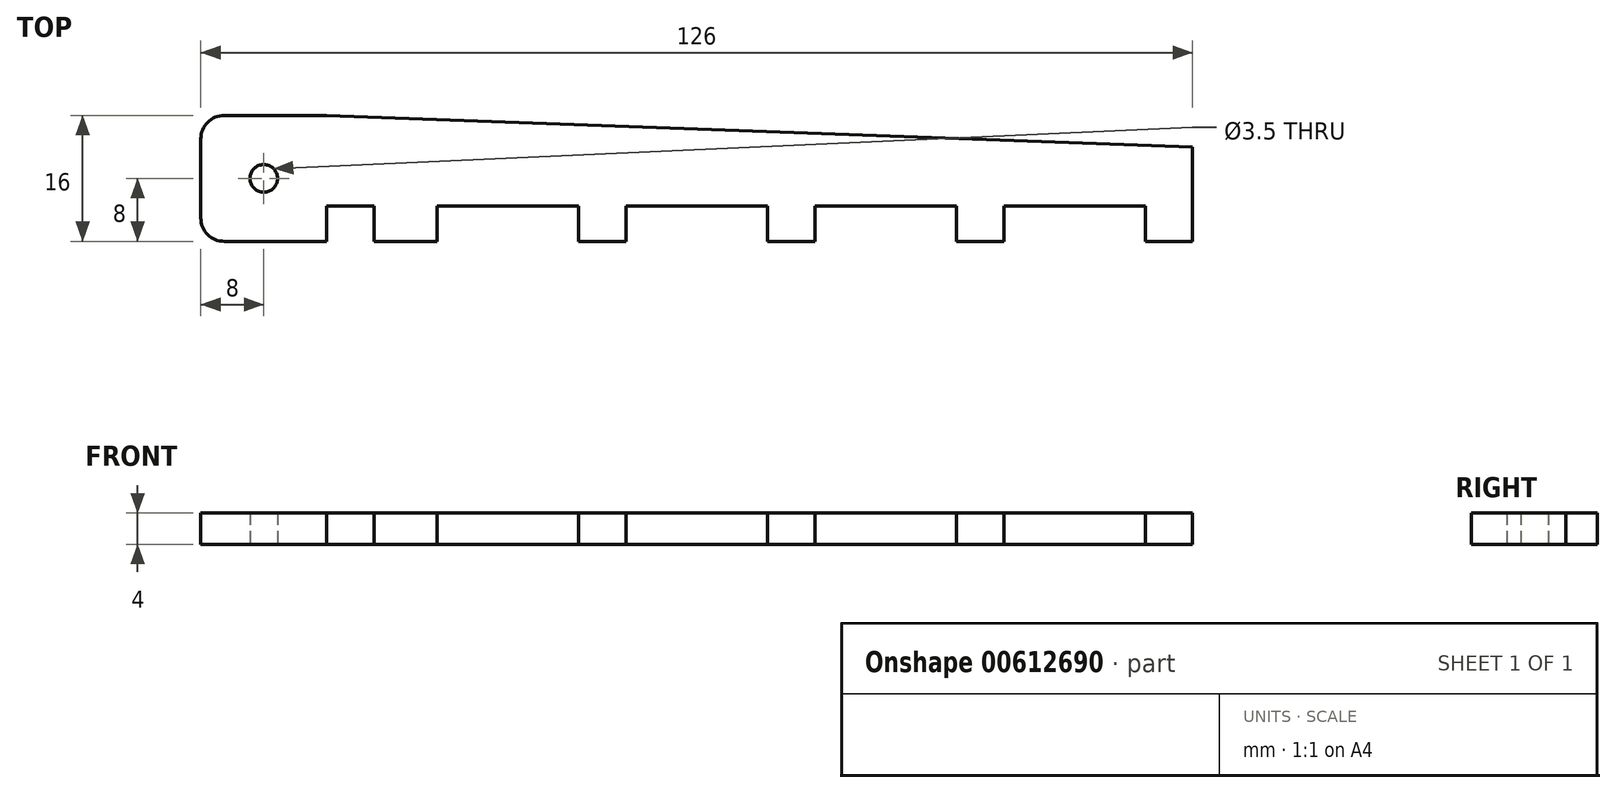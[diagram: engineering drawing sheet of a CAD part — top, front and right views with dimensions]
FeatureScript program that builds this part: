
annotation { "Feature Type Name" : "Feature", "Feature Type Description" : "" }
export const myFeature = defineFeature(function(context is Context, id is Id, definition is map)
    precondition{}
    {
        {
            var Q0;
            Q0=qCreatedBy(makeId("Top.planeOp"),FACE);
            var sketch = newSketch(context, id + "F0", { "sketchPlane" : qUnion([Q0])});
            skLineSegment(sketch, "E0", {"start": v(-9, -8) * mm, "end": v(-15, -8) * mm});
            skLineSegment(sketch, "E1", {"start": v(15, -8) * mm, "end": v(9, -8) * mm});
            skLineSegment(sketch, "E2", {"start": v(63, -8) * mm, "end": v(57, -8) * mm});
            skLineSegment(sketch, "E3", {"start": v(39, -8) * mm, "end": v(33, -8) * mm});
            skLineSegment(sketch, "E4", {"start": v(-47, -8) * mm, "end": v(-60, -8) * mm});
            skLineSegment(sketch, "E5", {"start": v(63, -8) * mm, "end": v(63, 4) * mm});
            skLineSegment(sketch, "E6", {"start": v(-41, -8) * mm, "end": v(-41, -3.5) * mm});
            skLineSegment(sketch, "E7", {"start": v(-15, -3.5) * mm, "end": v(-33, -3.5) * mm});
            skLineSegment(sketch, "E8", {"start": v(9, -3.5) * mm, "end": v(-9, -3.5) * mm});
            skLineSegment(sketch, "E9", {"start": v(57, -3.5) * mm, "end": v(39, -3.5) * mm});
            skLineSegment(sketch, "E10", {"start": v(33, -3.5) * mm, "end": v(15, -3.5) * mm});
            skLineSegment(sketch, "E11", {"start": v(-41, -3.5) * mm, "end": v(-47, -3.5) * mm});
            skLineSegment(sketch, "E12", {"start": v(-47, -8) * mm, "end": v(-47, -3.5) * mm});
            skLineSegment(sketch, "E13", {"start": v(-33, -8) * mm, "end": v(-33, -3.5) * mm});
            skLineSegment(sketch, "E14", {"start": v(57, -8) * mm, "end": v(57, -3.5) * mm});
            skLineSegment(sketch, "E15", {"start": v(39, -8) * mm, "end": v(39, -3.5) * mm});
            skLineSegment(sketch, "E16", {"start": v(-15, -8) * mm, "end": v(-15, -3.5) * mm});
            skLineSegment(sketch, "E17", {"start": v(-9, -8) * mm, "end": v(-9, -3.5) * mm});
            skLineSegment(sketch, "E18", {"start": v(33, -8) * mm, "end": v(33, -3.5) * mm});
            skLineSegment(sketch, "E19", {"start": v(15, -8) * mm, "end": v(15, -3.5) * mm});
            skLineSegment(sketch, "E20", {"start": v(9, -8) * mm, "end": v(9, -3.5) * mm});
            skLineSegment(sketch, "E21", {"start": v(-63, -5) * mm, "end": v(-63, 5) * mm});
            skLineSegment(sketch, "E22", {"start": v(-47, 8) * mm, "end": v(-60, 8) * mm});
            skArc(sketch, "E23", {"start": v(-63, -5) * mm, "mid": v(-62.12, -7.12) * mm, "end": v(-60, -8) * mm});
            skArc(sketch, "E24", {"start": v(-60, 8) * mm, "mid": v(-62.12, 7.12) * mm, "end": v(-63, 5) * mm});
            skLineSegment(sketch, "E25", {"start": v(-47, 8) * mm, "end": v(63, 4) * mm});
            skLineSegment(sketch, "E26", {"start": v(-33, -8) * mm, "end": v(-41, -8) * mm});
            skCircle(sketch, "E27", {"center": v(-55, 0) * mm, "radius": 1.75 * mm});
            skSolve(sketch);
        }
        {
            var Q0;
            Q0=makeQuery(id+"F0.imprint","IMPRINT",FACE,{"disambiguationData":[TD([[makeQuery(id+"F0.imprint","IMPRINT",EDGE,{"derivedFrom":sQuery(id+"F0.wireOp",EDGE,"E0")}),-1.0]])]});
            extrude(context, id + "F1", {"entities" : qUnion([Q0]), "depth" : 4 * mm, "offsetDistance" : 25 * mm});
        }
    });
